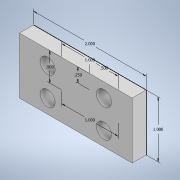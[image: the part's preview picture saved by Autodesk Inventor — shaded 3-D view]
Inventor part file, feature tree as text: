
AUTODESK INVENTOR PART (.ipt)
format: ipt  version: 2020 (Build 240168000, 168)  size: 109,568 bytes
history: native  units: in
note: dims shown in document units (in); Inventor stores cm internally (conversion verified against a paired STEP export)
features: sketch x1, extrude x1, hole x1
ambient origin geometry x8: Origin, YZ Plane, XZ Plane, XY Plane, X Axis, Y Axis, Z Axis, Center Point
bodies: Solid1 (feature_tree)
feature tree (3):
  sketch  "Sketch1"  dims[d0=2.0in d1=1.0in d2=0.25in d3=0.5in d4=1.0in d5=0.5in d6=1.0in d7=0.25in d8=0.0in d9=0.266in d10=0.75in d11=0.438in d12=0.25in d13=0.5635in d14=1.0in d15=0.8108in]
  extrude  "Extrusion1"  Depth=1.0in
  hole  "Hole1"  [1 undecoded]
note: 1 required parameter value undecoded (feature->parameter linkage not recoverable at this tier; creation-order binding heuristic only, values carry confidence <= 0.55)
